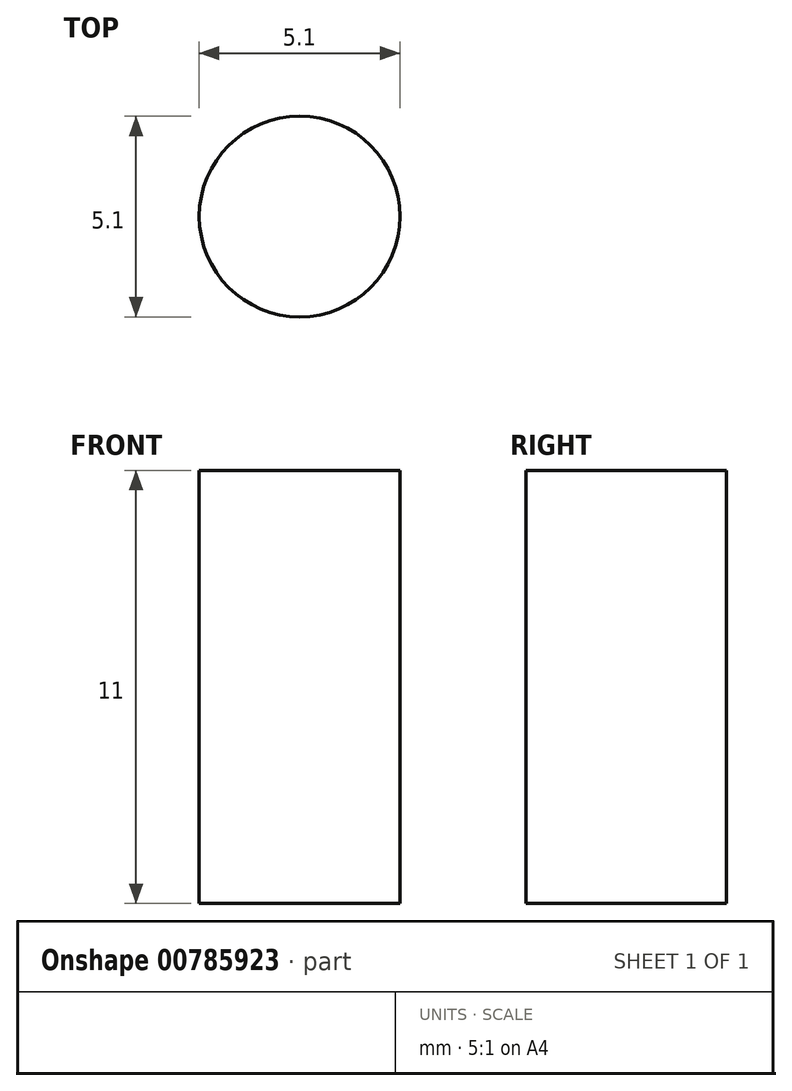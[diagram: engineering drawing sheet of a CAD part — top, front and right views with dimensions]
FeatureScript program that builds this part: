
annotation { "Feature Type Name" : "Feature", "Feature Type Description" : "" }
export const myFeature = defineFeature(function(context is Context, id is Id, definition is map)
    precondition{}
    {
        {
            var Q0;
            Q0=qCreatedBy(makeId("Top.planeOp"),FACE);
            var sketch = newSketch(context, id + "F0", { "sketchPlane" : qUnion([Q0])});
            skCircle(sketch, "E0", {"center": v(-38.49, -36.88) * mm, "radius": 2.55 * mm});
            skSolve(sketch);
        }
        {
            var Q0;
            Q0=makeQuery(id+"F0.imprint","IMPRINT",FACE,{"disambiguationData":[TD([[makeQuery(id+"F0.imprint","IMPRINT",EDGE,{"derivedFrom":sQuery(id+"F0.wireOp",EDGE,"E0")}),1.0]])]});
            extrude(context, id + "F1", {"entities" : qUnion([Q0]), "depth" : 11 * mm, "offsetDistance" : 25 * mm});
        }
    });
